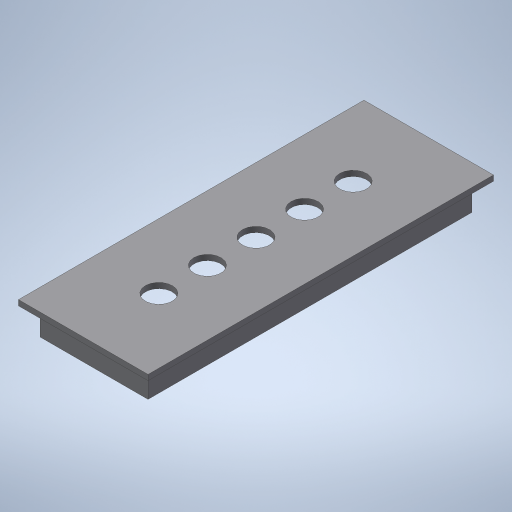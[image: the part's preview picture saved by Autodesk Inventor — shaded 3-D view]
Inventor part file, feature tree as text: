
AUTODESK INVENTOR PART (.ipt)
format: ipt  version: 2023.1 (Build 271208000, 208)  size: 248,832 bytes
history: native  units: mm
features: extrude x3, sketch x3, projected_geometry x2
ambient origin geometry x8: Origin, YZ Plane, XZ Plane, XY Plane, X Axis, Y Axis, Z Axis, Center Point
bodies: Solid1 (feature_tree)
feature tree (8):
  extrude  "Extrusion1"  Depth=64.0mm
  extrude  "Extrusion2"  Depth=2.0mm
  extrude  "Extrusion3"  Depth=5.0mm TaperAngle=0.0deg
  sketch  "Sketch1"  dims[d0=24.0mm d1=64.0mm]
  sketch  "Sketch2"  dims[d2=1.0mm d3=0.0mm d4=2.0mm]
  projected_geometry  "Projected Loop1"
  sketch  "Sketch3"  dims[d5=2.0mm d6=5.0mm d7=0.0mm d8=1.0mm d9=1.0mm d10=9.0mm d11=9.0mm d12=9.0mm d13=9.0mm d14=9.0mm d15=5.0mm d16=5.0mm d17=5.0mm d18=5.0mm d19=5.0mm d20=2.0mm d21=0.0mm]
  projected_geometry  "Projected Loop2"
